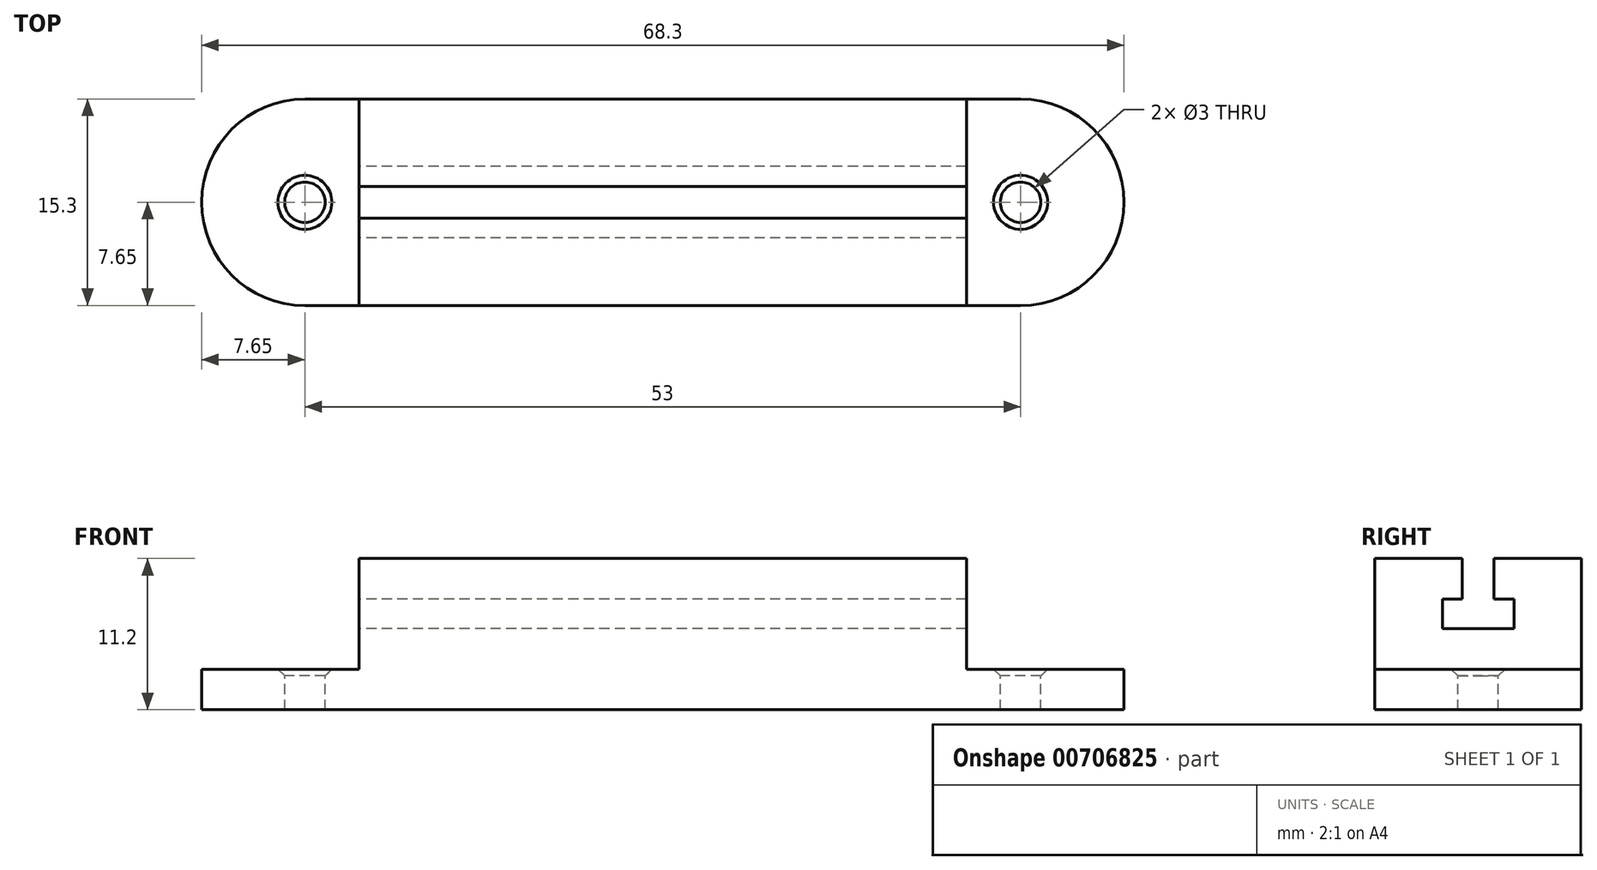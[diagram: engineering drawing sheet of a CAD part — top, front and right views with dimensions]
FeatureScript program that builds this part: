
annotation { "Feature Type Name" : "Feature", "Feature Type Description" : "" }
export const myFeature = defineFeature(function(context is Context, id is Id, definition is map)
    precondition{}
    {
        {
            var Q0;
            Q0=qCreatedBy(makeId("Right.planeOp"),FACE);
            var sketch = newSketch(context, id + "F0", { "sketchPlane" : qUnion([Q0])});
            skLineSegment(sketch, "E0.right", {"start": v(7.65, 11.2) * mm, "end": v(7.65, 0) * mm});
            skLineSegment(sketch, "E1.right", {"start": v(1.17, 11.2) * mm, "end": v(1.17, 8.2) * mm});
            skLineSegment(sketch, "E2.right", {"start": v(2.65, 8.2) * mm, "end": v(2.65, 6) * mm});
            skLineSegment(sketch, "E3.trimOffspring", {"start": v(1.17, 8.2) * mm, "end": v(2.65, 8.2) * mm});
            skLineSegment(sketch, "E4.trimOffspring", {"start": v(1.17, 11.2) * mm, "end": v(7.65, 11.2) * mm});
            skLineSegment(sketch, "E5", {"start": v(0, 0) * mm, "end": v(0, 6) * mm});
            skLineSegment(sketch, "E6", {"start": v(0, 6) * mm, "end": v(2.65, 6) * mm});
            skLineSegment(sketch, "E7", {"start": v(0, 0) * mm, "end": v(7.65, 0) * mm});
            skLineSegment(sketch, "E8", {"start": v(0, 0) * mm, "end": v(0, 34.97) * mm, "construction": true});
            skLineSegment(sketch, "E9.MirrorCS", {"start": v(-1.17, 11.2) * mm, "end": v(-7.65, 11.2) * mm});
            skLineSegment(sketch, "E10.MirrorCS", {"start": v(-1.17, 11.2) * mm, "end": v(-1.17, 8.2) * mm});
            skLineSegment(sketch, "E11.MirrorCS", {"start": v(0, 0) * mm, "end": v(-7.65, 0) * mm});
            skLineSegment(sketch, "E12.MirrorCS", {"start": v(-1.17, 8.2) * mm, "end": v(-2.65, 8.2) * mm});
            skLineSegment(sketch, "E13.MirrorCS", {"start": v(-7.65, 11.2) * mm, "end": v(-7.65, 0) * mm});
            skLineSegment(sketch, "E14.MirrorCS", {"start": v(0, 6) * mm, "end": v(-2.65, 6) * mm});
            skLineSegment(sketch, "E15.MirrorCS", {"start": v(-2.65, 8.2) * mm, "end": v(-2.65, 6) * mm});
            skSolve(sketch);
        }
        {
            var Q0;
            Q0=makeQuery(id+"F0.imprint","IMPRINT",FACE,{"disambiguationData":[TD([[makeQuery(id+"F0.imprint","IMPRINT",EDGE,{"derivedFrom":sQuery(id+"F0.wireOp",EDGE,"E0.right")}),-1.0]])]});
            var Q1;
            Q1=makeQuery(id+"F0.imprint","IMPRINT",FACE,{"disambiguationData":[TD([[makeQuery(id+"F0.imprint","IMPRINT",EDGE,{"derivedFrom":sQuery(id+"F0.wireOp",EDGE,"E5")}),1.0]])]});
            extrude(context, id + "F1", {"entities" : qUnion([Q0, Q1]), "endBound" : BoundingType.SYMMETRIC, "depth" : 45 * mm, "offsetDistance" : 25 * mm});
        }
        {
            var Q0;
            Q0=makeQuery(id+"F1.opExtrude","SWEPT_FACE",FACE,{"disambiguationData":[OSD([sQuery(id+"F0.wireOp",EDGE,"E7"),sQuery(id+"F0.wireOp",EDGE,"E11.MirrorCS")])]});
            var sketch = newSketch(context, id + "F2", { "sketchPlane" : qUnion([Q0])});
            skLineSegment(sketch, "E16", {"start": v(0, -40.33) * mm, "end": v(0, 39.65) * mm, "construction": true});
            skLineSegment(sketch, "E17.bottom", {"start": v(22.5, -7.65) * mm, "end": v(26.5, -7.65) * mm});
            skLineSegment(sketch, "E17.top", {"start": v(22.5, 7.65) * mm, "end": v(26.5, 7.65) * mm});
            skLineSegment(sketch, "E17.left", {"start": v(22.5, -7.65) * mm, "end": v(22.5, 7.65) * mm});
            skArc(sketch, "E18", {"start": v(26.5, -7.65) * mm, "mid": v(34.15, 0) * mm, "end": v(26.5, 7.65) * mm});
            skLineSegment(sketch, "E19.MirrorCS", {"start": v(-22.5, -7.65) * mm, "end": v(-22.5, 7.65) * mm});
            skLineSegment(sketch, "E20.MirrorCS", {"start": v(-22.5, -7.65) * mm, "end": v(-26.5, -7.65) * mm});
            skLineSegment(sketch, "E21.MirrorCS", {"start": v(-22.5, 7.65) * mm, "end": v(-26.5, 7.65) * mm});
            skArc(sketch, "E22.MirrorCS", {"start": v(-26.5, -7.65) * mm, "mid": v(-34.15, 0) * mm, "end": v(-26.5, 7.65) * mm});
            skCircle(sketch, "E23", {"center": v(26.5, 0) * mm, "radius": 1.5 * mm, "construction": true});
            skCircle(sketch, "E24.MirrorC", {"center": v(-26.5, 0) * mm, "radius": 1.5 * mm, "construction": true});
            skSolve(sketch);
        }
        {
            var Q0;
            Q0=makeQuery(id+"F2.imprint","IMPRINT",FACE,{"disambiguationData":[TD([[makeQuery(id+"F2.imprint","IMPRINT",EDGE,{"derivedFrom":sQuery(id+"F2.wireOp",EDGE,"E17.bottom")}),1.0]])]});
            var Q1;
            Q1=makeQuery(id+"F2.imprint","IMPRINT",FACE,{"disambiguationData":[TD([[makeQuery(id+"F2.imprint","IMPRINT",EDGE,{"derivedFrom":sQuery(id+"F2.wireOp",EDGE,"E19.MirrorCS")}),-1.0]])]});
            extrude(context, id + "F3", {"entities" : qUnion([Q0, Q1]), "operationType" : NewBodyOperationType.ADD, "oppositeDirection" : true, "depth" : 3 * mm, "offsetDistance" : 25 * mm});
        }
        {
            var Q0;
            Q0=makeQuery(id+"F3.opExtrude","CAP_FACE",FACE,{"disambiguationData":[OSD([sQuery(id+"F2.wireOp",EDGE,"E19.MirrorCS"),sQuery(id+"F2.wireOp",EDGE,"E20.MirrorCS"),sQuery(id+"F2.wireOp",EDGE,"E21.MirrorCS"),sQuery(id+"F2.wireOp",EDGE,"E22.MirrorCS")])],"isStart":false});
            var sketch = newSketch(context, id + "F4", { "sketchPlane" : qUnion([Q0])});
            skLineSegment(sketch, "E25.0.0", {"start": v(26.5, -7.65) * mm, "end": v(-26.5, -7.65) * mm});
            skArc(sketch, "E25.0.1", {"start": v(-26.5, -7.65) * mm, "mid": v(-34.15, 0) * mm, "end": v(-26.5, 7.65) * mm});
            skLineSegment(sketch, "E25.0.2", {"start": v(-26.5, 7.65) * mm, "end": v(26.5, 7.65) * mm});
            skArc(sketch, "E25.0.3", {"start": v(26.5, 7.65) * mm, "mid": v(34.15, 0) * mm, "end": v(26.5, -7.65) * mm});
            skSolve(sketch);
        }
        {
            var Q0;
            Q0=sQuery(id+"F4.wireOp",VERTEX,"E25.0.3.center");
            var Q1;
            Q1=sQuery(id+"F4.wireOp",VERTEX,"E25.0.1.center");
            var Q2;
            Q2=makeQuery(id+"F1.opExtrude","SWEPT_BODY",BODY,{"disambiguationData":[OSD([sQuery(id+"F0.wireOp",EDGE,"E0.right"),sQuery(id+"F0.wireOp",EDGE,"E1.right"),sQuery(id+"F0.wireOp",EDGE,"E2.right"),sQuery(id+"F0.wireOp",EDGE,"E3.trimOffspring"),sQuery(id+"F0.wireOp",EDGE,"E4.trimOffspring"),sQuery(id+"F0.wireOp",EDGE,"E6"),sQuery(id+"F0.wireOp",EDGE,"E7"),sQuery(id+"F0.wireOp",EDGE,"E9.MirrorCS"),sQuery(id+"F0.wireOp",EDGE,"E10.MirrorCS"),sQuery(id+"F0.wireOp",EDGE,"E11.MirrorCS"),sQuery(id+"F0.wireOp",EDGE,"E12.MirrorCS"),sQuery(id+"F0.wireOp",EDGE,"E13.MirrorCS"),sQuery(id+"F0.wireOp",EDGE,"E14.MirrorCS"),sQuery(id+"F0.wireOp",EDGE,"E15.MirrorCS")])]});
            hole(context, id + "F5", {"style" : HoleStyle.C_SINK, "endStyle" : HoleEndStyle.BLIND, "holeDiameter" : 3 * mm, "cSinkDiameter" : 4 * mm, "cSinkAngle" : 90 * degree, "majorDiameter" : 5 * mm, "holeDepth" : 4 * mm, "isTappedThrough" : true, "tappedDepth" : 12 * mm, "tapClearance" : 3, "locations" : qUnion([Q0, Q1]), "scope" : qUnion([Q2])});
        }
    });
